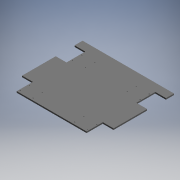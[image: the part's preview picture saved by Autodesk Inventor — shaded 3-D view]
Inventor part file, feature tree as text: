
AUTODESK INVENTOR PART (.ipt)
format: ipt  version: 2019 (Build 230136000, 136)  size: 153,600 bytes
history: native  units: mm (DEFAULTED — no unit token found)
features: sketch x3, extrude x2, hole x1, plane x1, mirror x1
ambient origin geometry x8: Origin, YZ Plane, XZ Plane, XY Plane, X Axis, Y Axis, Z Axis, Center Point
bodies: Solid1 (feature_tree)
feature tree (8):
  extrude  "Extrusion1"  Depth=361.95mm
  extrude  "Extrusion3"  Depth=76.2mm
  hole  "Hole1"  [1 undecoded]
  plane  "Work Plane1"
  mirror  "Mirror1"
  sketch  "Sketch1"  dims[d0=431.8mm d1=361.95mm]
  sketch  "Sketch3"  dims[d2=6.35mm d3=0.0mm d11=76.2mm]
  sketch  "Sketch4"  dims[d12=88.9mm d13=127.0mm d14=50.8mm d15=50.8mm d16=6.35mm d17=0.0mm d18=60.8076mm d19=5.9944mm d20=103.8098mm d21=5.9944mm d22=66.9036mm d23=60.8076mm d24=103.8098mm d25=66.9036mm d26=5.9944mm d27=10.4902mm d28=5.9944mm d29=53.4924mm d30=66.9036mm d31=66.9036mm d32=10.4902mm d33=53.4924mm d34=3.81mm d35=19.05mm d36=9.525mm d37=6.35mm d38=14.3117mm d39=25.4mm d40=20.594885mm]
note: 1 required parameter value undecoded (feature->parameter linkage not recoverable at this tier; creation-order binding heuristic only, values carry confidence <= 0.55)
